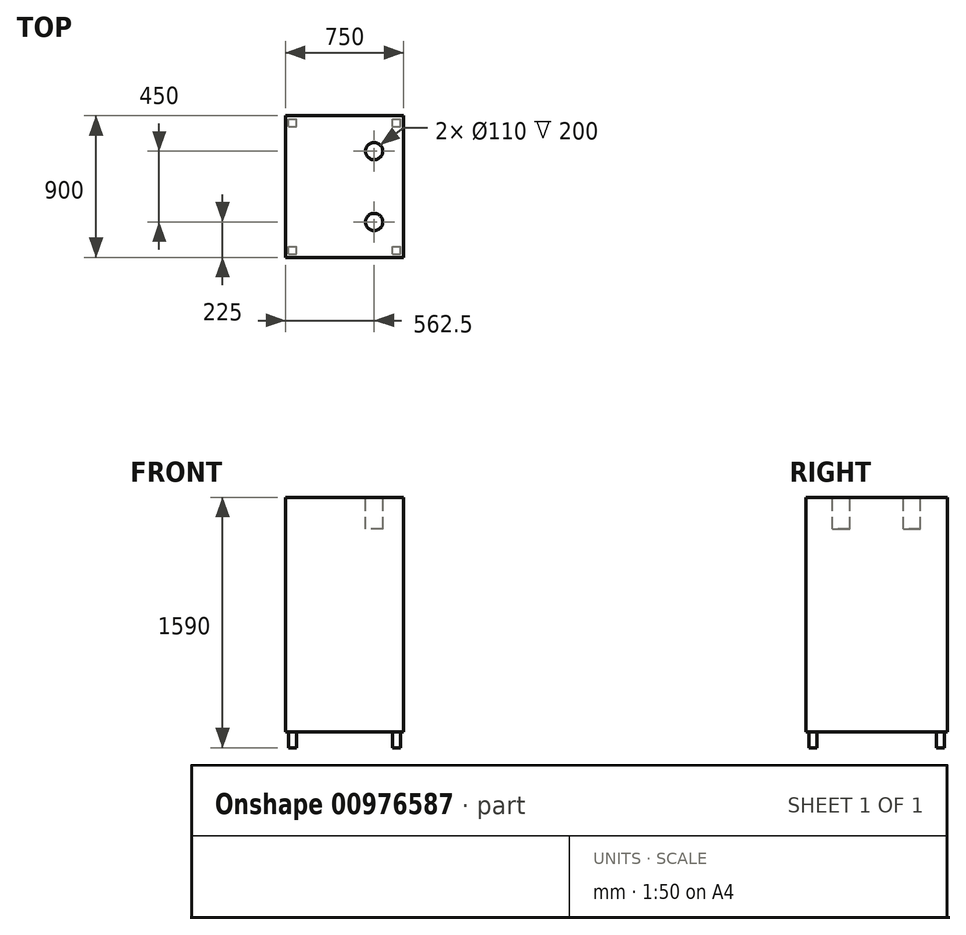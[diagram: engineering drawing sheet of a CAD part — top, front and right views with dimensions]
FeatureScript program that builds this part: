
annotation { "Feature Type Name" : "Feature", "Feature Type Description" : "" }
export const myFeature = defineFeature(function(context is Context, id is Id, definition is map)
    precondition{}
    {
        {
            var Q0;
            Q0=qCreatedBy(makeId("Top.planeOp"),FACE);
            var sketch = newSketch(context, id + "F0", { "sketchPlane" : qUnion([Q0])});
            skLineSegment(sketch, "E0.bottom", {"start": v(375, 450) * mm, "end": v(-375, 450) * mm});
            skLineSegment(sketch, "E0.top", {"start": v(375, -450) * mm, "end": v(-375, -450) * mm});
            skLineSegment(sketch, "E0.left", {"start": v(375, 450) * mm, "end": v(375, -450) * mm});
            skLineSegment(sketch, "E0.right", {"start": v(-375, 450) * mm, "end": v(-375, -450) * mm});
            skPoint(sketch, "E0.middle", {"position": v(0, 0) * mm});
            skSolve(sketch);
        }
        {
            var Q0;
            Q0 = qSketchRegion(id + "F0", true);
            extrude(context, id + "F1", {"entities" : qUnion([Q0]), "oppositeDirection" : true, "depth" : 1490 * mm, "offsetDistance" : 25 * mm});
        }
        {
            var Q0;
            Q0=makeQuery(id+"F1.opExtrude","CAP_FACE",FACE,{"disambiguationData":[OSD([sQuery(id+"F0.wireOp",EDGE,"E0.bottom"),sQuery(id+"F0.wireOp",EDGE,"E0.top"),sQuery(id+"F0.wireOp",EDGE,"E0.left"),sQuery(id+"F0.wireOp",EDGE,"E0.right")])],"isStart":false});
            var sketch = newSketch(context, id + "F2", { "sketchPlane" : qUnion([Q0])});
            skLineSegment(sketch, "E1.bottom", {"start": v(-355, 430) * mm, "end": v(-305, 430) * mm});
            skLineSegment(sketch, "E1.top", {"start": v(-355, 380) * mm, "end": v(-305, 380) * mm});
            skLineSegment(sketch, "E1.left", {"start": v(-355, 430) * mm, "end": v(-355, 380) * mm});
            skLineSegment(sketch, "E1.right", {"start": v(-305, 430) * mm, "end": v(-305, 380) * mm});
            skLineSegment(sketch, "E2.bottom", {"start": v(305, 430) * mm, "end": v(355, 430) * mm});
            skLineSegment(sketch, "E2.top", {"start": v(305, 380) * mm, "end": v(355, 380) * mm});
            skLineSegment(sketch, "E2.left", {"start": v(305, 430) * mm, "end": v(305, 380) * mm});
            skLineSegment(sketch, "E2.right", {"start": v(355, 430) * mm, "end": v(355, 380) * mm});
            skLineSegment(sketch, "E3.bottom", {"start": v(-355, -380) * mm, "end": v(-305, -380) * mm});
            skLineSegment(sketch, "E3.top", {"start": v(-355, -430) * mm, "end": v(-305, -430) * mm});
            skLineSegment(sketch, "E3.left", {"start": v(-355, -380) * mm, "end": v(-355, -430) * mm});
            skLineSegment(sketch, "E3.right", {"start": v(-305, -380) * mm, "end": v(-305, -430) * mm});
            skLineSegment(sketch, "E4.bottom", {"start": v(305, -380) * mm, "end": v(355, -380) * mm});
            skLineSegment(sketch, "E4.top", {"start": v(305, -430) * mm, "end": v(355, -430) * mm});
            skLineSegment(sketch, "E4.left", {"start": v(305, -380) * mm, "end": v(305, -430) * mm});
            skLineSegment(sketch, "E4.right", {"start": v(355, -380) * mm, "end": v(355, -430) * mm});
            skSolve(sketch);
        }
        {
            var Q0;
            Q0 = qSketchRegion(id + "F2", true);
            extrude(context, id + "F3", {"entities" : qUnion([Q0]), "operationType" : NewBodyOperationType.ADD, "depth" : 100 * mm, "offsetDistance" : 25 * mm});
        }
        {
            var Q0;
            Q0=makeQuery(id+"F1.opExtrude","CAP_FACE",FACE,{"disambiguationData":[OSD([sQuery(id+"F0.wireOp",EDGE,"E0.bottom"),sQuery(id+"F0.wireOp",EDGE,"E0.top"),sQuery(id+"F0.wireOp",EDGE,"E0.left"),sQuery(id+"F0.wireOp",EDGE,"E0.right")])],"isStart":true});
            var sketch = newSketch(context, id + "F4", { "sketchPlane" : qUnion([Q0])});
            skLineSegment(sketch, "E5", {"start": v(0, 450) * mm, "end": v(0, -450) * mm, "construction": true});
            skLineSegment(sketch, "E6", {"start": v(187.5, 450) * mm, "end": v(187.5, -450) * mm, "construction": true});
            skLineSegment(sketch, "E7", {"start": v(-375, 0) * mm, "end": v(375, 0) * mm, "construction": true});
            skLineSegment(sketch, "E8", {"start": v(375, 225) * mm, "end": v(-375, 225) * mm, "construction": true});
            skLineSegment(sketch, "E9", {"start": v(375, -225) * mm, "end": v(-375, -225) * mm, "construction": true});
            skCircle(sketch, "E10", {"center": v(187.5, 225) * mm, "radius": 55 * mm});
            skCircle(sketch, "E11", {"center": v(187.5, -225) * mm, "radius": 55 * mm});
            skSolve(sketch);
        }
        {
            var Q0;
            Q0 = qSketchRegion(id + "F4", true);
            extrude(context, id + "F5", {"entities" : qUnion([Q0]), "operationType" : NewBodyOperationType.REMOVE, "oppositeDirection" : true, "depth" : 200 * mm, "offsetDistance" : 25 * mm});
        }
    });
